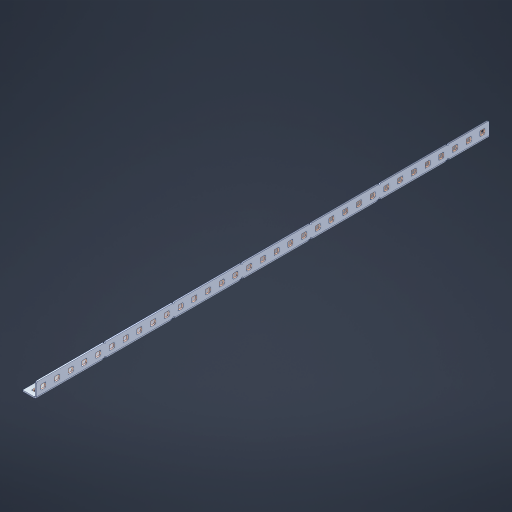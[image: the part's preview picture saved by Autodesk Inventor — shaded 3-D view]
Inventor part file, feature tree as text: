
AUTODESK INVENTOR PART (.ipt)
format: ipt  version: 2023 (Build 270158000, 158)  size: 1,004,032 bytes
history: native  units: in
note: dims shown in document units (in); Inventor stores cm internally (conversion verified against a paired STEP export)
features: other x71, extrude x65, sheet_metal_op x10, sketch x8, mirror x1, pattern_linear x1, chamfer x1
ambient origin geometry x8: Origin, YZ Plane, XZ Plane, XY Plane, X Axis, Y Axis, Z Axis, Center Point
bodies: Solid1 (feature_tree), Body (feature_tree)
feature tree (157):
  other  "Flange Pattern Plane"
  sheet_metal_op  "Flange Pattern"
  sheet_metal_op  "Body Pattern"
  other  "Arc Length"
  mirror  "Notch Mirror"
  pattern_linear  "Notch Pattern"  Spacing1=0.1875in  [1 undecoded]
  chamfer  "End Chamfer"
  extrude  "Half Cut"  Depth=0.0469in
  sketch  "Sketch1"  dims[d0=2.5in]
  other  "Plate1"
  sketch  "Sketch2"  dims[d1=16.5in]
  other  "Plate2"
  sheet_metal_op  "Bend1"
  sheet_metal_op  "Corner1"
  sketch  "Sketch3"  dims[d2=0.0469in]
  other  "Flange Pattern Sketch"
  sketch  "Sketch7"  dims[d3=0.0469in]
  other  "Srf1"
  other  "Srf2"
  sketch  "Sketch8"  dims[d4=0.0234in]
  sketch  "Sketch9"  dims[d5=0.0938in]
  other  "Srf91"
  sheet_metal_op  "Body Pattern Sketch"
  other  "Srf92"
  sketch  "Sketch13"  dims[d6=0.0469in]
  sketch  "Sketch14"  dims[d7=0.5in d8=90.0deg d9=0.0312in d10=0.1875in d11=0.0469in d12=0.0469in d16=0.182in d17=0.02in d18=0.0469in d19=0.0in d20=0.25in d21=0.25in d46=0.172in d47=1.0in d48=0.0in d49=0.182in d50=0.02in d51=0.25in d52=0.25in d53=0.0469in d54=0.0in d55=0.172in d56=1.0in d57=0.0in d60=12.9921in d62=0.5in d63=0.3937in d65=0.5in d85=0.1227in d86=0.1659in d88=0.04in d89=0.0469in d90=0.0in d91=0.04in d92=0.0491in d95=2.5in d96=0.04in d97=0.25in d98=45.0deg d101=0.0in d102=2.497in d131=0.5in d132=12.9921in d134=0.5in d139=0.5in]
  other  "Srf856"
  other  "Srf1310"
  other  "Srf1311"
  other  "Srf1312"
  other  "Srf1376"
  other  "Srf1377"
  other  "Srf1728"
  other  "Srf1755"
  other  "Srf1878"
  other  "Srf1879"
  other  "Srf1880"
  other  "Srf1881"
  other  "Srf1882"
  other  "Srf1883"
  other  "Srf1884"
  other  "Srf1885"
  other  "Srf1886"
  other  "Srf1887"
  other  "Srf1888"
  other  "Srf1889"
  other  "Srf1890"
  other  "Srf1891"
  other  "Srf1892"
  other  "Srf1893"
  other  "Srf1894"
  other  "Srf1895"
  other  "Srf1896"
  other  "Srf1897"
  other  "Srf1898"
  other  "Srf1899"
  other  "Srf1900"
  other  "Srf1901"
  other  "Srf1902"
  other  "Srf1903"
  other  "Srf1904"
  other  "Srf1942"
  other  "Srf1943"
  other  "Srf1944"
  other  "Srf1945"
  other  "Srf1946"
  other  "Srf1947"
  other  "Srf1948"
  other  "Srf1949"
  other  "Srf1950"
  other  "Srf1951"
  other  "Srf1952"
  other  "Srf1953"
  other  "Srf1954"
  other  "Srf1955"
  other  "Srf1956"
  other  "Srf1957"
  other  "Srf1958"
  other  "Srf1959"
  other  "Srf1960"
  other  "Srf1961"
  other  "Srf1962"
  other  "Srf1963"
  other  "Srf1964"
  other  "Srf1965"
  other  "Srf1966"
  other  "Srf1967"
  other  "Srf1968"
  sheet_metal_op  "Flange Stamp"
  sheet_metal_op  "Flange Circle"
  sheet_metal_op  "Body Stamp"
  sheet_metal_op  "Body Circle"
  sheet_metal_op  "Notch"
  extrude  "ExtrusionSrf2"  Depth=0.0469in
  extrude  "ExtrusionSrf92"  Depth=0.5in
  extrude  "ExtrusionSrf856"  Depth=0.02in
  extrude  "ExtrusionSrf1310"  Depth=0.0469in
  extrude  "ExtrusionSrf1311"  TaperAngle=0.0deg  [1 undecoded]
  extrude  "ExtrusionSrf1312"  Depth=0.5in
  extrude  "ExtrusionSrf1376"  Depth=0.5in
  extrude  "ExtrusionSrf1377"  Depth=0.5in
  extrude  "ExtrusionSrf1728"  Depth=0.5in TaperAngle=0.0deg
  extrude  "ExtrusionSrf1755"  Depth=0.5in
  extrude  "ExtrusionSrf1878"  Depth=0.02in
  extrude  "ExtrusionSrf1879"  Depth=0.5in
  extrude  "ExtrusionSrf1880"  Depth=0.5in
  extrude  "ExtrusionSrf1881"  Depth=0.0469in
  extrude  "ExtrusionSrf1882"  TaperAngle=0.0deg  [1 undecoded]
  extrude  "ExtrusionSrf1883"  Depth=0.5in
  extrude  "ExtrusionSrf1884"  Depth=0.5in TaperAngle=0.0deg
  extrude  "ExtrusionSrf1885"  Depth=0.5in
  extrude  "ExtrusionSrf1886"  Depth=0.5in
  extrude  "ExtrusionSrf1887"  Depth=0.5in
  extrude  "ExtrusionSrf1888"  Depth=0.5in
  extrude  "ExtrusionSrf1889"  Depth=0.5in
  extrude  "ExtrusionSrf1890"  Depth=0.0469in
  extrude  "ExtrusionSrf1891"  TaperAngle=0.0deg  [1 undecoded]
  extrude  "ExtrusionSrf1892"  Depth=0.5in
  extrude  "ExtrusionSrf1893"  Depth=0.5in
  extrude  "ExtrusionSrf1894"  Depth=0.5in
  extrude  "ExtrusionSrf1895"  Depth=0.5in TaperAngle=45.0deg
  extrude  "ExtrusionSrf1896"  TaperAngle=0.0deg  [1 undecoded]
  extrude  "ExtrusionSrf1897"  Depth=0.5in
  extrude  "ExtrusionSrf1898"  Depth=0.5in
  extrude  "ExtrusionSrf1899"  Depth=0.5in
  extrude  "ExtrusionSrf1900"  Depth=0.5in
  extrude  "ExtrusionSrf1901"  Depth=0.5in
  extrude  "ExtrusionSrf1902"  [1 undecoded]
  extrude  "ExtrusionSrf1903"  [1 undecoded]
  extrude  "ExtrusionSrf1904"  [1 undecoded]
  extrude  "ExtrusionSrf1942"  [1 undecoded]
  extrude  "ExtrusionSrf1943"  [1 undecoded]
  extrude  "ExtrusionSrf1944"  [1 undecoded]
  extrude  "ExtrusionSrf1945"  [1 undecoded]
  extrude  "ExtrusionSrf1946"  [1 undecoded]
  extrude  "ExtrusionSrf1947"  [1 undecoded]
  extrude  "ExtrusionSrf1948"  [1 undecoded]
  extrude  "ExtrusionSrf1949"  [1 undecoded]
  extrude  "ExtrusionSrf1950"  [1 undecoded]
  extrude  "ExtrusionSrf1951"  [1 undecoded]
  extrude  "ExtrusionSrf1952"  [1 undecoded]
  extrude  "ExtrusionSrf1953"  [1 undecoded]
  extrude  "ExtrusionSrf1954"  [1 undecoded]
  extrude  "ExtrusionSrf1955"  [1 undecoded]
  extrude  "ExtrusionSrf1956"  [1 undecoded]
  extrude  "ExtrusionSrf1957"  [1 undecoded]
  extrude  "ExtrusionSrf1958"  [1 undecoded]
  extrude  "ExtrusionSrf1959"  [1 undecoded]
  extrude  "ExtrusionSrf1960"  [1 undecoded]
  extrude  "ExtrusionSrf1961"  [1 undecoded]
  extrude  "ExtrusionSrf1962"  [1 undecoded]
  extrude  "ExtrusionSrf1963"  [1 undecoded]
  extrude  "ExtrusionSrf1964"  [1 undecoded]
  extrude  "ExtrusionSrf1965"  [1 undecoded]
  extrude  "ExtrusionSrf1966"  [1 undecoded]
  extrude  "ExtrusionSrf1967"  [1 undecoded]
  extrude  "ExtrusionSrf1968"  [1 undecoded]
note: 35 required parameter values undecoded (feature->parameter linkage not recoverable at this tier; creation-order binding heuristic only, values carry confidence <= 0.55)
